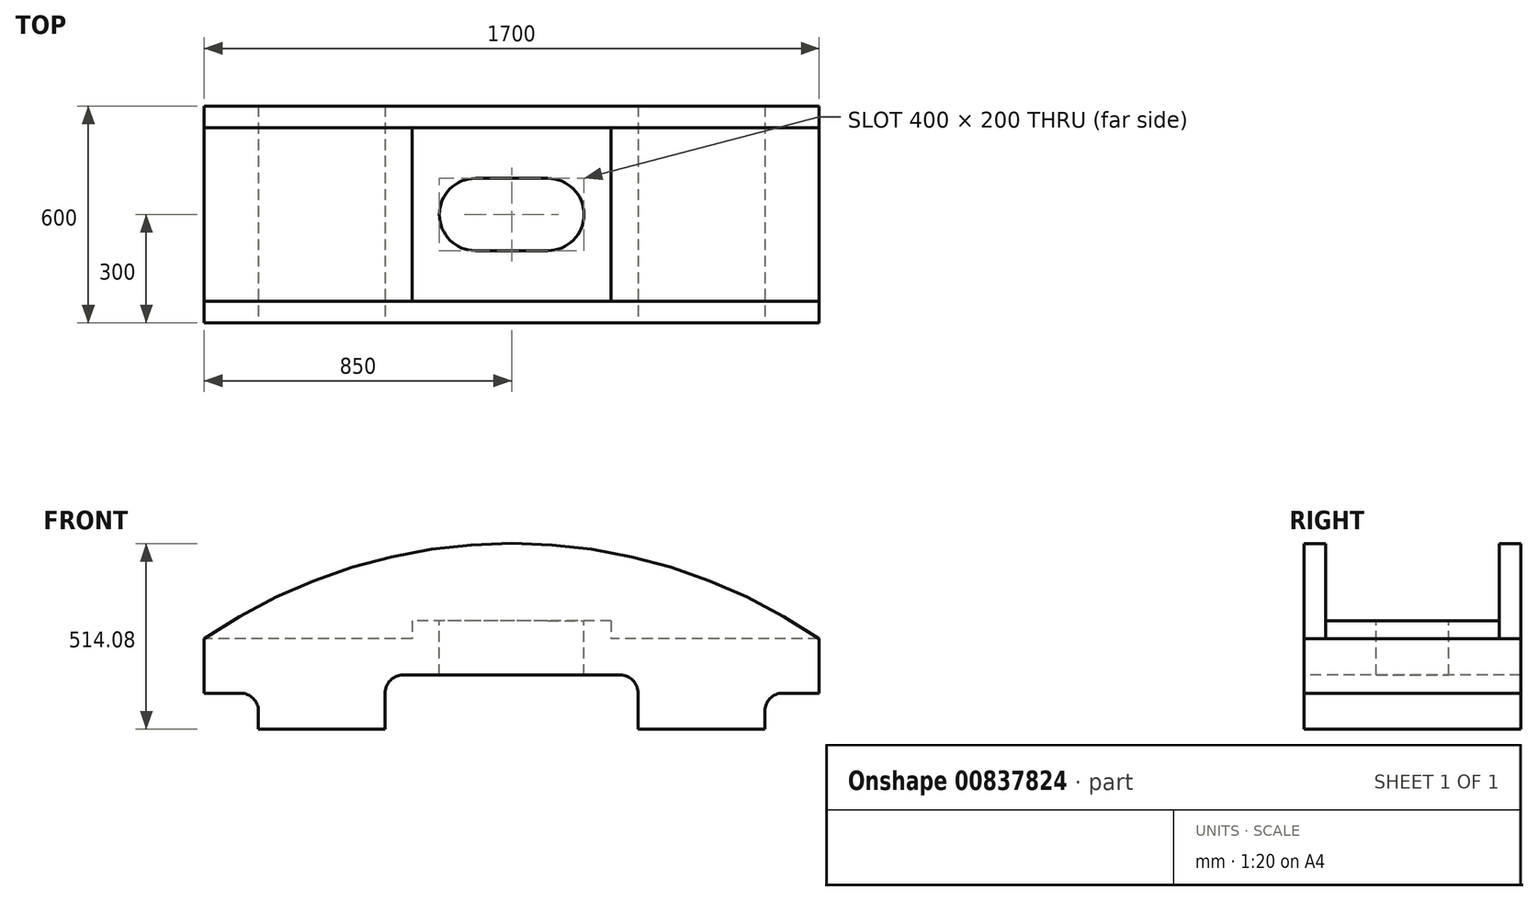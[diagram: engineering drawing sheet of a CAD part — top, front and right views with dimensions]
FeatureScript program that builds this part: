
annotation { "Feature Type Name" : "Feature", "Feature Type Description" : "" }
export const myFeature = defineFeature(function(context is Context, id is Id, definition is map)
    precondition{}
    {
        {
            var Q0;
            Q0=qCreatedBy(makeId("Top.planeOp"),FACE);
            var sketch = newSketch(context, id + "F0", { "sketchPlane" : qUnion([Q0])});
            skLineSegment(sketch, "E0.bottom", {"start": v(850, -300) * mm, "end": v(-850, -300) * mm});
            skLineSegment(sketch, "E0.top", {"start": v(850, 300) * mm, "end": v(-850, 300) * mm});
            skLineSegment(sketch, "E0.left", {"start": v(850, -300) * mm, "end": v(850, 300) * mm});
            skLineSegment(sketch, "E0.right", {"start": v(-850, -300) * mm, "end": v(-850, 300) * mm});
            skPoint(sketch, "E0.middle", {"position": v(0, 0) * mm});
            skSolve(sketch);
        }
        {
            var Q0;
            Q0=makeQuery(id+"F0.imprint","IMPRINT",FACE,{"disambiguationData":[TD([[makeQuery(id+"F0.imprint","IMPRINT",EDGE,{"derivedFrom":sQuery(id+"F0.wireOp",EDGE,"E0.bottom")}),-1.0]])]});
            extrude(context, id + "F1", {"entities" : qUnion([Q0]), "depth" : 250 * mm, "offsetDistance" : 25 * mm});
        }
        {
            var Q0;
            Q0=makeQuery(id+"F1.opExtrude","CAP_FACE",FACE,{"disambiguationData":[OSD([sQuery(id+"F0.wireOp",EDGE,"E0.bottom"),sQuery(id+"F0.wireOp",EDGE,"E0.top"),sQuery(id+"F0.wireOp",EDGE,"E0.left"),sQuery(id+"F0.wireOp",EDGE,"E0.right")])],"isStart":false});
            var sketch = newSketch(context, id + "F2", { "sketchPlane" : qUnion([Q0])});
            skLineSegment(sketch, "E1.bottom", {"start": v(275, -240) * mm, "end": v(-275, -240) * mm});
            skLineSegment(sketch, "E1.top", {"start": v(275, 240) * mm, "end": v(-275, 240) * mm});
            skLineSegment(sketch, "E1.left", {"start": v(275, -240) * mm, "end": v(275, 240) * mm});
            skLineSegment(sketch, "E1.right", {"start": v(-275, -240) * mm, "end": v(-275, 240) * mm});
            skPoint(sketch, "E1.middle", {"position": v(0, 0) * mm});
            skSolve(sketch);
        }
        {
            var Q0;
            Q0=makeQuery(id+"F2.imprint","IMPRINT",FACE,{"disambiguationData":[TD([[makeQuery(id+"F2.imprint","IMPRINT",EDGE,{"derivedFrom":sQuery(id+"F2.wireOp",EDGE,"E1.bottom")}),-1.0]])]});
            extrude(context, id + "F3", {"entities" : qUnion([Q0]), "operationType" : NewBodyOperationType.ADD, "depth" : 50 * mm, "offsetDistance" : 25 * mm});
        }
        {
            var Q0;
            Q0=makeQuery(id+"F3.opExtrude","CAP_FACE",FACE,{"disambiguationData":[OSD([sQuery(id+"F2.wireOp",EDGE,"E1.bottom"),sQuery(id+"F2.wireOp",EDGE,"E1.top"),sQuery(id+"F2.wireOp",EDGE,"E1.left"),sQuery(id+"F2.wireOp",EDGE,"E1.right")])],"isStart":false});
            var sketch = newSketch(context, id + "F4", { "sketchPlane" : qUnion([Q0])});
            skLineSegment(sketch, "E2.bottom", {"start": v(100, -100) * mm, "end": v(-100, -100) * mm});
            skLineSegment(sketch, "E2.top", {"start": v(100, 100) * mm, "end": v(-100, 100) * mm});
            skLineSegment(sketch, "E2.left", {"start": v(100, -100) * mm, "end": v(100, 100) * mm});
            skLineSegment(sketch, "E2.right", {"start": v(-100, -100) * mm, "end": v(-100, 100) * mm});
            skPoint(sketch, "E2.middle", {"position": v(0, 0) * mm});
            skCircle(sketch, "E3", {"center": v(-100, 0) * mm, "radius": 100 * mm});
            skCircle(sketch, "E4", {"center": v(100, 0) * mm, "radius": 100 * mm});
            skSolve(sketch);
        }
        {
            var Q0;
            {var subQ0=sQuery(id+"F4.wireOp",EDGE,"E2.right");Q0=makeQuery(id+"F4.imprint","IMPRINT",FACE,{"disambiguationData":[TD([[makeQuery(id+"F4.imprint","IMPRINT",EDGE,{"derivedFrom":subQ0}),1.0]])]});}
            var Q1;
            {var subQ0=sQuery(id+"F4.wireOp",EDGE,"E2.right");Q1=makeQuery(id+"F4.imprint","IMPRINT",FACE,{"disambiguationData":[TD([[makeQuery(id+"F4.imprint","IMPRINT",EDGE,{"derivedFrom":subQ0}),-1.0]])]});}
            var Q2;
            {var subQ0=sQuery(id+"F4.wireOp",EDGE,"E2.left");Q2=makeQuery(id+"F4.imprint","IMPRINT",FACE,{"disambiguationData":[TD([[makeQuery(id+"F4.imprint","IMPRINT",EDGE,{"derivedFrom":subQ0}),1.0]])]});}
            var Q3;
            {var subQ0=sQuery(id+"F4.wireOp",EDGE,"E2.left");Q3=makeQuery(id+"F4.imprint","IMPRINT",FACE,{"disambiguationData":[TD([[makeQuery(id+"F4.imprint","IMPRINT",EDGE,{"derivedFrom":subQ0}),-1.0]])]});}
            var Q4;
            {var subQ0=sQuery(id+"F4.wireOp",EDGE,"E2.top");Q4=makeQuery(id+"F4.imprint","IMPRINT",FACE,{"disambiguationData":[TD([[makeQuery(id+"F4.imprint","IMPRINT",EDGE,{"derivedFrom":subQ0}),1.0]])]});}
            var Q5;
            {var subQ0=sQuery(id+"F4.wireOp",EDGE,"E2.bottom");Q5=makeQuery(id+"F4.imprint","IMPRINT",FACE,{"disambiguationData":[TD([[makeQuery(id+"F4.imprint","IMPRINT",EDGE,{"derivedFrom":subQ0}),-1.0]])]});}
            extrude(context, id + "F5", {"entities" : qUnion([Q0, Q1, Q2, Q3, Q4, Q5]), "operationType" : NewBodyOperationType.REMOVE, "endBound" : BoundingType.THROUGH_ALL, "oppositeDirection" : true, "depth" : 25 * mm, "offsetDistance" : 25 * mm});
        }
        {
            var Q0;
            Q0=makeQuery(id+"F1.opExtrude","SWEPT_FACE",FACE,{"disambiguationData":[OSD([sQuery(id+"F0.wireOp",EDGE,"E0.bottom")])]});
            var sketch = newSketch(context, id + "F6", { "sketchPlane" : qUnion([Q0])});
            skLineSegment(sketch, "E5", {"start": v(0, 0) * mm, "end": v(-350, 0) * mm});
            skLineSegment(sketch, "E6", {"start": v(0, 0) * mm, "end": v(350, 0) * mm});
            skLineSegment(sketch, "E7", {"start": v(0, 0) * mm, "end": v(0, 150) * mm});
            skLineSegment(sketch, "E8", {"start": v(-350, 0) * mm, "end": v(-350, 100) * mm});
            skLineSegment(sketch, "E9", {"start": v(-300, 150) * mm, "end": v(300, 150) * mm});
            skLineSegment(sketch, "E10", {"start": v(350, 100) * mm, "end": v(350, 0) * mm});
            skPoint(sketch, "E11.visualSharp", {"position": v(-350, 150) * mm});
            skArc(sketch, "E11.filletArc", {"start": v(-300, 150) * mm, "mid": v(-335.36, 135.36) * mm, "end": v(-350, 100) * mm});
            skPoint(sketch, "E12.visualSharp", {"position": v(350, 150) * mm});
            skArc(sketch, "E12.filletArc", {"start": v(350, 100) * mm, "mid": v(335.36, 135.36) * mm, "end": v(300, 150) * mm});
            skSolve(sketch);
        }
        {
            var Q0;
            Q0=makeQuery(id+"F6.imprint","IMPRINT",FACE,{"disambiguationData":[TD([[makeQuery(id+"F6.imprint","IMPRINT",EDGE,{"derivedFrom":sQuery(id+"F6.wireOp",EDGE,"E5")}),-1.0]])]});
            var Q1;
            Q1=makeQuery(id+"F6.imprint","IMPRINT",FACE,{"disambiguationData":[TD([[makeQuery(id+"F6.imprint","IMPRINT",EDGE,{"derivedFrom":sQuery(id+"F6.wireOp",EDGE,"E6")}),-1.0]])]});
            extrude(context, id + "F7", {"entities" : qUnion([Q0, Q1]), "operationType" : NewBodyOperationType.REMOVE, "endBound" : BoundingType.THROUGH_ALL, "oppositeDirection" : true, "depth" : 25 * mm, "offsetDistance" : 25 * mm});
        }
        {
            var Q0;
            Q0=makeQuery(id+"F1.opExtrude","SWEPT_FACE",FACE,{"disambiguationData":[OSD([sQuery(id+"F0.wireOp",EDGE,"E0.bottom")])]});
            var sketch = newSketch(context, id + "F8", { "sketchPlane" : qUnion([Q0])});
            skLineSegment(sketch, "E13", {"start": v(-850, 0) * mm, "end": v(-700, 0) * mm});
            skLineSegment(sketch, "E14", {"start": v(850, 0) * mm, "end": v(700, 0) * mm});
            skLineSegment(sketch, "E15", {"start": v(-850, 0) * mm, "end": v(-850, 100) * mm});
            skLineSegment(sketch, "E16", {"start": v(850, 0) * mm, "end": v(850, 100) * mm});
            skLineSegment(sketch, "E17", {"start": v(-850, 100) * mm, "end": v(-750, 100) * mm});
            skLineSegment(sketch, "E18", {"start": v(-700, 50) * mm, "end": v(-700, 0) * mm});
            skLineSegment(sketch, "E19", {"start": v(700, 0) * mm, "end": v(700, 50) * mm});
            skLineSegment(sketch, "E20", {"start": v(750, 100) * mm, "end": v(850, 100) * mm});
            skPoint(sketch, "E21.visualSharp", {"position": v(-700, 100) * mm});
            skArc(sketch, "E21.filletArc", {"start": v(-700, 50) * mm, "mid": v(-714.64, 85.36) * mm, "end": v(-750, 100) * mm});
            skPoint(sketch, "E22.visualSharp", {"position": v(700, 100) * mm});
            skArc(sketch, "E22.filletArc", {"start": v(750, 100) * mm, "mid": v(714.64, 85.36) * mm, "end": v(700, 50) * mm});
            skSolve(sketch);
        }
        {
            var Q0;
            Q0=makeQuery(id+"F8.imprint","IMPRINT",FACE,{"disambiguationData":[TD([[makeQuery(id+"F8.imprint","IMPRINT",EDGE,{"derivedFrom":sQuery(id+"F8.wireOp",EDGE,"E14")}),-1.0]])]});
            var Q1;
            Q1=makeQuery(id+"F8.imprint","IMPRINT",FACE,{"disambiguationData":[TD([[makeQuery(id+"F8.imprint","IMPRINT",EDGE,{"derivedFrom":sQuery(id+"F8.wireOp",EDGE,"E13")}),-1.0]])]});
            extrude(context, id + "F9", {"entities" : qUnion([Q0, Q1]), "operationType" : NewBodyOperationType.REMOVE, "endBound" : BoundingType.THROUGH_ALL, "oppositeDirection" : true, "depth" : 25 * mm, "offsetDistance" : 25 * mm});
        }
        {
            var Q0;
            Q0=makeQuery(id+"F1.opExtrude","SWEPT_FACE",FACE,{"disambiguationData":[OSD([sQuery(id+"F0.wireOp",EDGE,"E0.bottom")])]});
            var sketch = newSketch(context, id + "F10", { "sketchPlane" : qUnion([Q0])});
            skArc(sketch, "E23", {"start": v(850, 250) * mm, "mid": v(0, 514.08) * mm, "end": v(-850, 250) * mm});
            skSolve(sketch);
        }
        {
            var Q0;
            Q0=makeQuery(id+"F1.opExtrude","SWEPT_FACE",FACE,{"disambiguationData":[OSD([sQuery(id+"F0.wireOp",EDGE,"E0.top")])]});
            var sketch = newSketch(context, id + "F11", { "sketchPlane" : qUnion([Q0])});
            skArc(sketch, "E24", {"start": v(850, 250) * mm, "mid": v(0, 514.08) * mm, "end": v(-850, 250) * mm});
            skSolve(sketch);
        }
        {
            var Q0;
            Q0=makeQuery(id+"F11.imprint","IMPRINT",FACE,{"disambiguationData":[TD([[makeQuery(id+"F11.imprint","IMPRINT",EDGE,{"derivedFrom":sQuery(id+"F11.wireOp",EDGE,"E24")}),1.0]])]});
            extrude(context, id + "F12", {"entities" : qUnion([Q0]), "operationType" : NewBodyOperationType.ADD, "oppositeDirection" : true, "depth" : 60 * mm, "offsetDistance" : 25 * mm});
        }
        {
            var Q0;
            Q0=makeQuery(id+"F10.imprint","IMPRINT",FACE,{"disambiguationData":[TD([[makeQuery(id+"F10.imprint","IMPRINT",EDGE,{"derivedFrom":sQuery(id+"F10.wireOp",EDGE,"E23")}),1.0]])]});
            extrude(context, id + "F13", {"entities" : qUnion([Q0]), "operationType" : NewBodyOperationType.ADD, "oppositeDirection" : true, "depth" : 60 * mm, "offsetDistance" : 25 * mm});
        }
    });
